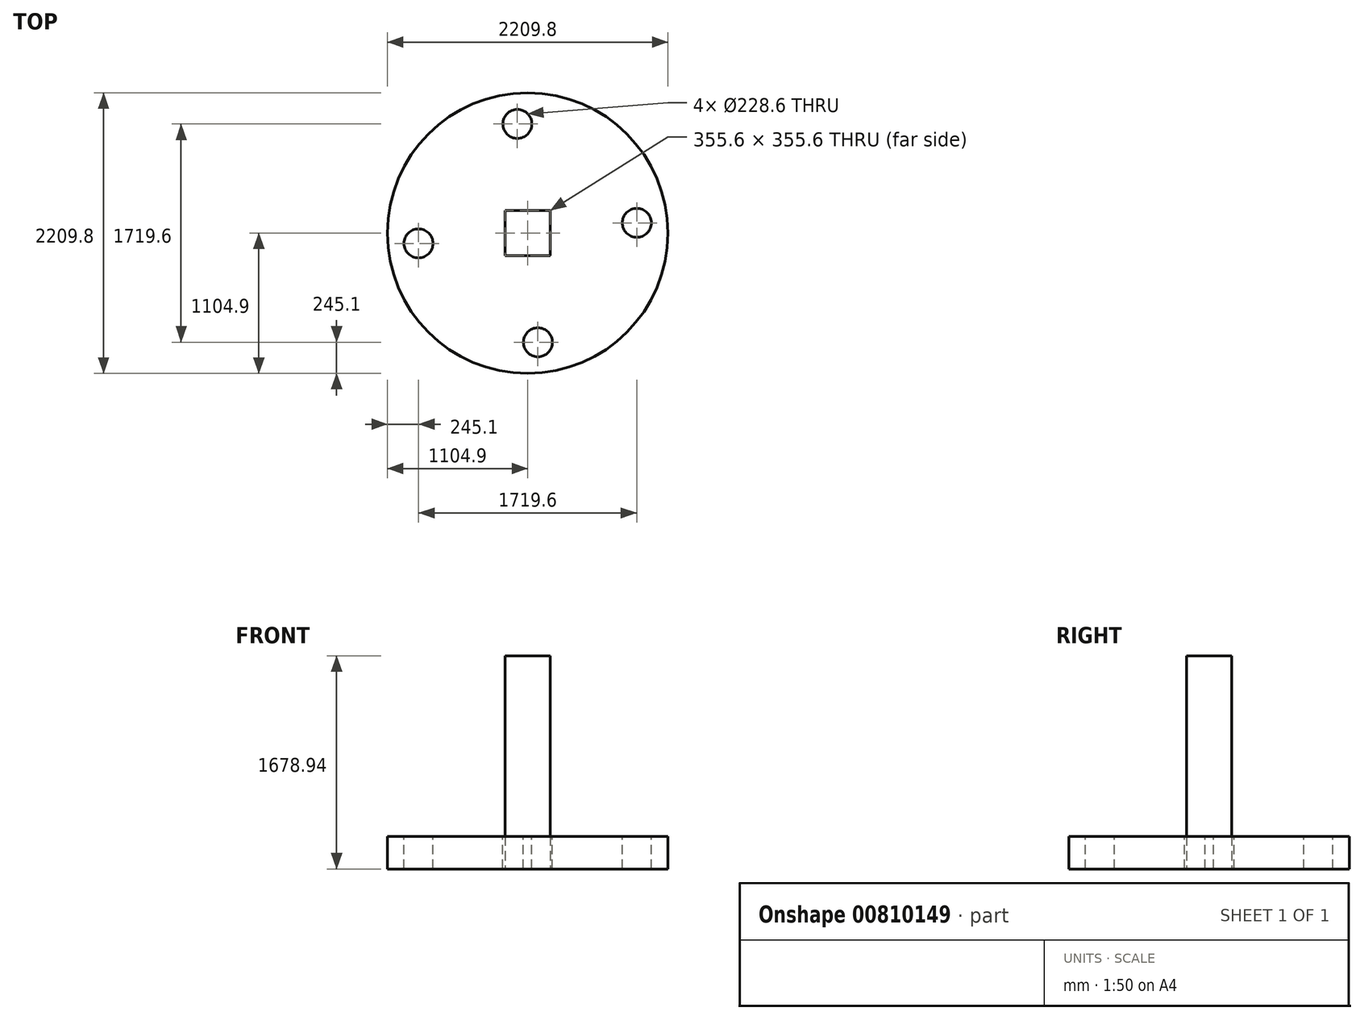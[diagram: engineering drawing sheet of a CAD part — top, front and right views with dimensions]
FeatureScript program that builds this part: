
annotation { "Feature Type Name" : "Feature", "Feature Type Description" : "" }
export const myFeature = defineFeature(function(context is Context, id is Id, definition is map)
    precondition{}
    {
        {
            var Q0;
            Q0=qCreatedBy(makeId("Top.planeOp"),FACE);
            var sketch = newSketch(context, id + "F0", { "sketchPlane" : qUnion([Q0])});
            skCircle(sketch, "E0", {"center": v(0, 0) * mm, "radius": 1104.9 * mm});
            skLineSegment(sketch, "E1.bottom", {"start": v(177.8, 177.8) * mm, "end": v(-177.8, 177.8) * mm});
            skLineSegment(sketch, "E1.top", {"start": v(177.8, -177.8) * mm, "end": v(-177.8, -177.8) * mm});
            skLineSegment(sketch, "E1.left", {"start": v(177.8, 177.8) * mm, "end": v(177.8, -177.8) * mm});
            skLineSegment(sketch, "E1.right", {"start": v(-177.8, 177.8) * mm, "end": v(-177.8, -177.8) * mm});
            skSolve(sketch);
        }
        {
            var Q0;
            Q0=makeQuery(id+"F0.imprint","IMPRINT",FACE,{"disambiguationData":[TD([[makeQuery(id+"F0.imprint","IMPRINT",EDGE,{"derivedFrom":sQuery(id+"F0.wireOp",EDGE,"E0")}),1.0]])]});
            extrude(context, id + "F1", {"entities" : qUnion([Q0]), "depth" : 256.54 * mm, "offsetDistance" : 25.4 * mm});
        }
        {
            var Q0;
            Q0=makeQuery(id+"F1.opExtrude","CAP_FACE",FACE,{"disambiguationData":[OSD([sQuery(id+"F0.wireOp",EDGE,"E0"),sQuery(id+"F0.wireOp",EDGE,"E1.bottom"),sQuery(id+"F0.wireOp",EDGE,"E1.top"),sQuery(id+"F0.wireOp",EDGE,"E1.left"),sQuery(id+"F0.wireOp",EDGE,"E1.right")])],"isStart":false});
            var sketch = newSketch(context, id + "F2", { "sketchPlane" : qUnion([Q0])});
            skLineSegment(sketch, "E2", {"start": v(0, 0) * mm, "end": v(-1104.9, 0) * mm});
            skLineSegment(sketch, "E3", {"start": v(-1104.9, 0) * mm, "end": v(-863.6, 0) * mm});
            skCircle(sketch, "E4", {"center": v(0, 0) * mm, "radius": 863.6 * mm});
            skCircle(sketch, "E5.cCircle", {"center": v(0, 0) * mm, "radius": 863.6 * mm, "construction": true});
            skLineSegment(sketch, "E5.0", {"start": v(-80.92, 859.8) * mm, "end": v(859.8, 80.92) * mm, "construction": true});
            skLineSegment(sketch, "E5.1", {"start": v(859.8, 80.92) * mm, "end": v(80.92, -859.8) * mm, "construction": true});
            skLineSegment(sketch, "E5.2", {"start": v(80.92, -859.8) * mm, "end": v(-859.8, -80.92) * mm, "construction": true});
            skLineSegment(sketch, "E5.3", {"start": v(-859.8, -80.92) * mm, "end": v(-80.92, 859.8) * mm, "construction": true});
            skCircle(sketch, "E6", {"center": v(-80.92, 859.8) * mm, "radius": 114.3 * mm});
            skCircle(sketch, "E7", {"center": v(-859.8, -80.92) * mm, "radius": 114.3 * mm});
            skCircle(sketch, "E8", {"center": v(80.92, -859.8) * mm, "radius": 114.3 * mm});
            skCircle(sketch, "E9", {"center": v(859.8, 80.92) * mm, "radius": 114.3 * mm});
            skSolve(sketch);
        }
        {
            var Q0;
            {var subQ0=sQuery(id+"F2.wireOp",EDGE,"E6");var subQ1=sQuery(id+"F2.wireOp",EDGE,"E4");var subQ2=makeQuery(id+"F2.imprint","INTERSECT",VERTEX,{"disambiguationData":[OD(0.0)],"derivedFrom":[subQ1,subQ0]});Q0=makeQuery(id+"F2.imprint","IMPRINT",FACE,{"disambiguationData":[TD([[makeQuery(id+"F2.imprint","IMPRINT",EDGE,{"disambiguationData":[TD([[subQ2,-1.0]])],"derivedFrom":subQ1}),1.0]])]});}
            var Q1;
            {var subQ0=sQuery(id+"F2.wireOp",EDGE,"E6");var subQ1=sQuery(id+"F2.wireOp",EDGE,"E4");var subQ2=makeQuery(id+"F2.imprint","INTERSECT",VERTEX,{"disambiguationData":[OD(0.0)],"derivedFrom":[subQ1,subQ0]});Q1=makeQuery(id+"F2.imprint","IMPRINT",FACE,{"disambiguationData":[TD([[makeQuery(id+"F2.imprint","IMPRINT",EDGE,{"disambiguationData":[TD([[subQ2,-1.0]])],"derivedFrom":subQ1}),-1.0]])]});}
            var Q2;
            {var subQ1=sQuery(id+"F2.wireOp",EDGE,"E3");var subQ3=sQuery(id+"F2.wireOp",EDGE,"E7");var subQ4=makeQuery(id+"F2.imprint","INTERSECT",VERTEX,{"derivedFrom":[subQ1,subQ3]});Q2=makeQuery(id+"F2.imprint","IMPRINT",FACE,{"disambiguationData":[TD([[makeQuery(id+"F2.imprint","IMPRINT",EDGE,{"disambiguationData":[TD([[subQ4,-1.0]])],"derivedFrom":subQ3}),1.0]])]});}
            var Q3;
            {var subQ1=sQuery(id+"F2.wireOp",EDGE,"E2");var subQ3=sQuery(id+"F2.wireOp",EDGE,"E7");var subQ4=makeQuery(id+"F2.imprint","INTERSECT",VERTEX,{"derivedFrom":[subQ1,subQ3]});Q3=makeQuery(id+"F2.imprint","IMPRINT",FACE,{"disambiguationData":[TD([[makeQuery(id+"F2.imprint","IMPRINT",EDGE,{"disambiguationData":[TD([[subQ4,1.0]])],"derivedFrom":subQ3}),1.0]])]});}
            var Q4;
            {var subQ0=sQuery(id+"F2.wireOp",EDGE,"E9");var subQ1=sQuery(id+"F2.wireOp",EDGE,"E4");var subQ2=makeQuery(id+"F2.imprint","INTERSECT",VERTEX,{"disambiguationData":[OD(0.0)],"derivedFrom":[subQ1,subQ0]});Q4=makeQuery(id+"F2.imprint","IMPRINT",FACE,{"disambiguationData":[TD([[makeQuery(id+"F2.imprint","IMPRINT",EDGE,{"disambiguationData":[TD([[subQ2,1.0]])],"derivedFrom":subQ1}),-1.0]])]});}
            var Q5;
            {var subQ0=sQuery(id+"F2.wireOp",EDGE,"E9");var subQ1=sQuery(id+"F2.wireOp",EDGE,"E4");var subQ2=makeQuery(id+"F2.imprint","INTERSECT",VERTEX,{"disambiguationData":[OD(0.0)],"derivedFrom":[subQ1,subQ0]});Q5=makeQuery(id+"F2.imprint","IMPRINT",FACE,{"disambiguationData":[TD([[makeQuery(id+"F2.imprint","IMPRINT",EDGE,{"disambiguationData":[TD([[subQ2,1.0]])],"derivedFrom":subQ1}),1.0]])]});}
            var Q6;
            {var subQ0=sQuery(id+"F2.wireOp",EDGE,"E8");var subQ1=sQuery(id+"F2.wireOp",EDGE,"E4");var subQ2=makeQuery(id+"F2.imprint","INTERSECT",VERTEX,{"disambiguationData":[OD(0.0)],"derivedFrom":[subQ1,subQ0]});Q6=makeQuery(id+"F2.imprint","IMPRINT",FACE,{"disambiguationData":[TD([[makeQuery(id+"F2.imprint","IMPRINT",EDGE,{"disambiguationData":[TD([[subQ2,-1.0]])],"derivedFrom":subQ1}),-1.0]])]});}
            var Q7;
            {var subQ0=sQuery(id+"F2.wireOp",EDGE,"E8");var subQ1=sQuery(id+"F2.wireOp",EDGE,"E4");var subQ2=makeQuery(id+"F2.imprint","INTERSECT",VERTEX,{"disambiguationData":[OD(0.0)],"derivedFrom":[subQ1,subQ0]});Q7=makeQuery(id+"F2.imprint","IMPRINT",FACE,{"disambiguationData":[TD([[makeQuery(id+"F2.imprint","IMPRINT",EDGE,{"disambiguationData":[TD([[subQ2,-1.0]])],"derivedFrom":subQ1}),1.0]])]});}
            var Q8;
            {var subQ1=sQuery(id+"F2.wireOp",EDGE,"E3");var subQ3=sQuery(id+"F2.wireOp",EDGE,"E7");var subQ4=makeQuery(id+"F2.imprint","INTERSECT",VERTEX,{"derivedFrom":[subQ1,subQ3]});Q8=makeQuery(id+"F2.imprint","IMPRINT",FACE,{"disambiguationData":[TD([[makeQuery(id+"F2.imprint","IMPRINT",EDGE,{"disambiguationData":[TD([[subQ4,1.0]])],"derivedFrom":subQ3}),1.0]])]});}
            var Q9;
            {var subQ1=sQuery(id+"F2.wireOp",EDGE,"E2");var subQ3=sQuery(id+"F2.wireOp",EDGE,"E7");var subQ4=makeQuery(id+"F2.imprint","INTERSECT",VERTEX,{"derivedFrom":[subQ1,subQ3]});Q9=makeQuery(id+"F2.imprint","IMPRINT",FACE,{"disambiguationData":[TD([[makeQuery(id+"F2.imprint","IMPRINT",EDGE,{"disambiguationData":[TD([[subQ4,-1.0]])],"derivedFrom":subQ3}),1.0]])]});}
            extrude(context, id + "F3", {"entities" : qUnion([Q0, Q1, Q2, Q3, Q4, Q5, Q6, Q7, Q8, Q9]), "operationType" : NewBodyOperationType.REMOVE, "oppositeDirection" : true, "depth" : 711.2 * mm, "offsetDistance" : 25.4 * mm});
        }
        {
            var Q0;
            {var subQ1=makeQuery(id+"F1.opExtrude","CAP_EDGE",EDGE,{"disambiguationData":[OSD([sQuery(id+"F0.wireOp",EDGE,"E1.bottom")])],"isStart":false});Q0=makeQuery(id+"F2.imprint","IMPRINT",FACE,{"disambiguationData":[TD([[makeQuery(id+"F2.imprint","IMPRINT",EDGE,{"derivedFrom":subQ1}),1.0]])]});}
            var sketch = newSketch(context, id + "F4", { "sketchPlane" : qUnion([Q0])});
            skSolve(sketch);
        }
        {
            var Q0;
            Q0 = qSketchRegion(id + "F4", true);
            var Q1;
            {var subQ1=makeQuery(id+"F1.opExtrude","CAP_EDGE",EDGE,{"disambiguationData":[OSD([sQuery(id+"F0.wireOp",EDGE,"E1.bottom")])],"isStart":false});Q1=makeQuery(id+"F4.imprint","IMPRINT",FACE,{"disambiguationData":[TD([[makeQuery(id+"F4.imprint","IMPRINT",EDGE,{"derivedFrom":makeQuery(id+"F2.imprint","IMPRINT",EDGE,{"derivedFrom":subQ1})}),1.0]])]});}
            extrude(context, id + "F5", {"entities" : qUnion([Q0, Q1]), "operationType" : NewBodyOperationType.ADD, "depth" : 1422.4 * mm, "offsetDistance" : 25.4 * mm});
        }
    });
